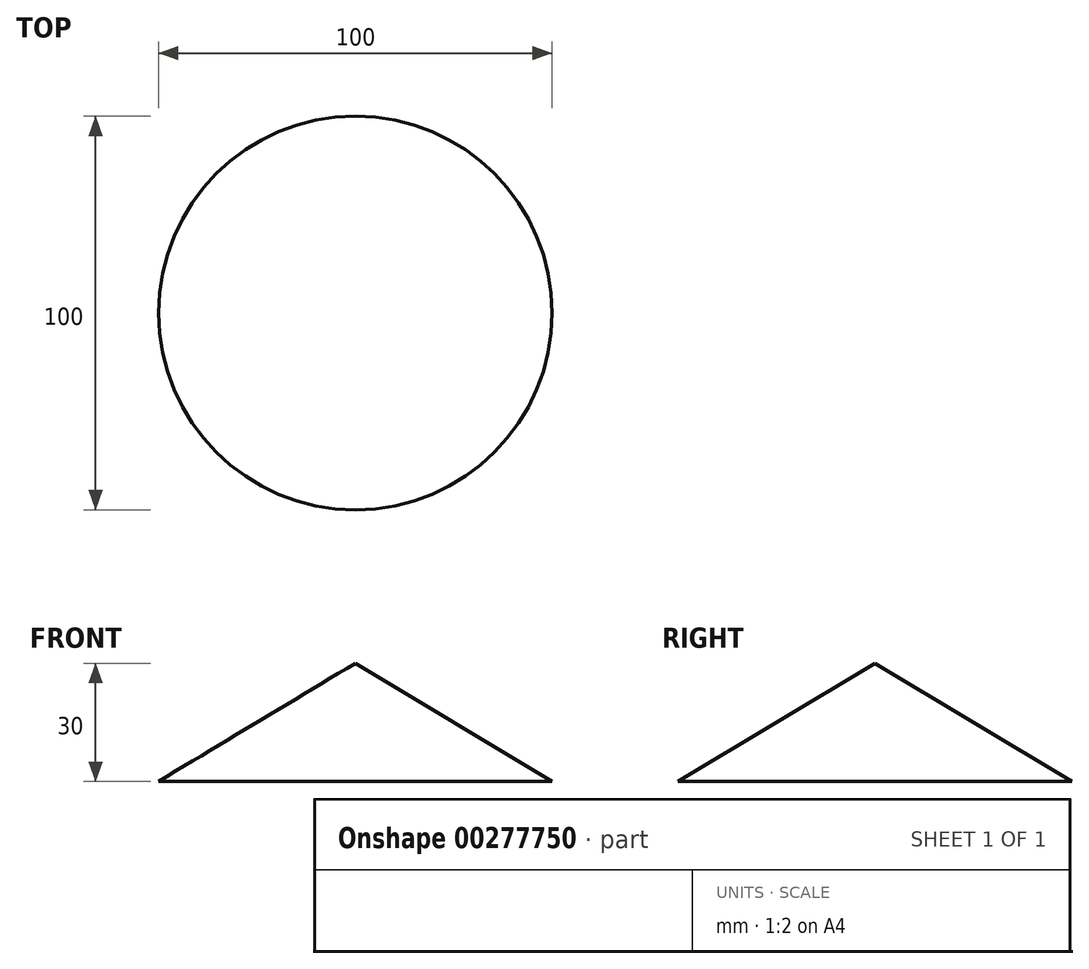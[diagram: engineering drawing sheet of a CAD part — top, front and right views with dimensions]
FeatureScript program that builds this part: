
annotation { "Feature Type Name" : "Feature", "Feature Type Description" : "" }
export const myFeature = defineFeature(function(context is Context, id is Id, definition is map)
    precondition{}
    {
        {
            var Q0;
            Q0=qCreatedBy(makeId("Front.planeOp"),FACE);
            var sketch = newSketch(context, id + "F0", { "sketchPlane" : qUnion([Q0])});
            skLineSegment(sketch, "E0.bottom", {"start": v(0, 0) * mm, "end": v(50, 0) * mm});
            skLineSegment(sketch, "E0.left", {"start": v(0, 0) * mm, "end": v(0, 30) * mm});
            skLineSegment(sketch, "E1", {"start": v(0, 30) * mm, "end": v(50, 0) * mm});
            skSolve(sketch);
        }
        {
            var Q0;
            Q0=qCreatedBy(makeId("Right.planeOp"),FACE);
            var sketch = newSketch(context, id + "F1", { "sketchPlane" : qUnion([Q0])});
            skLineSegment(sketch, "E2", {"start": v(0, 89.1) * mm, "end": v(0, 104.31) * mm, "construction": true});
            skSolve(sketch);
        }
        {
            var Q0;
            Q0=makeQuery(id+"F0.imprint","IMPRINT",FACE,{"disambiguationData":[TD([[makeQuery(id+"F0.imprint","IMPRINT",EDGE,{"derivedFrom":sQuery(id+"F0.wireOp",EDGE,"E0.bottom")}),1.0]])]});
            var Q1;
            Q1=sQuery(id+"F1.wireOp",EDGE,"E2");
            revolve(context, id + "F2", {"entities" : qUnion([Q0]), "axis" : qUnion([Q1]), "revolveType" : RevolveType.FULL});
        }
    });
